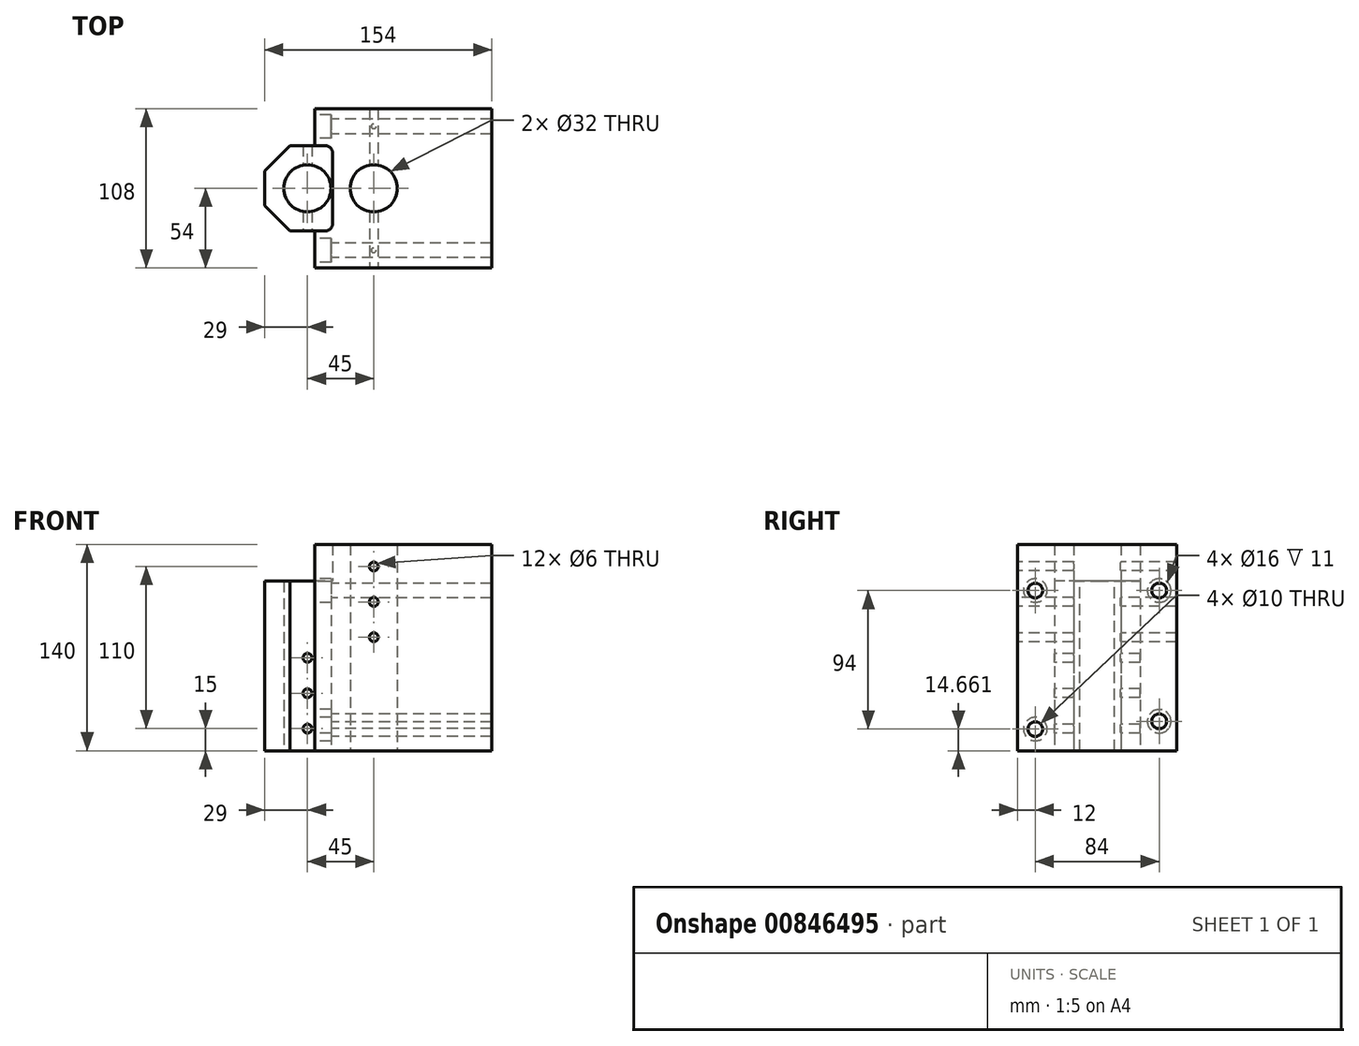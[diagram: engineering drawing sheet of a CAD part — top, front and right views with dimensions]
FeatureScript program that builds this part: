
annotation { "Feature Type Name" : "Feature", "Feature Type Description" : "" }
export const myFeature = defineFeature(function(context is Context, id is Id, definition is map)
    precondition{}
    {
        {
            var Q0;
            Q0=qCreatedBy(makeId("Front.planeOp"),FACE);
            var sketch = newSketch(context, id + "F0", { "sketchPlane" : qUnion([Q0])});
            skLineSegment(sketch, "E0.bottom", {"start": v(0, 77) * mm, "end": v(140, 77) * mm});
            skLineSegment(sketch, "E0.top", {"start": v(0, -77) * mm, "end": v(140, -77) * mm});
            skLineSegment(sketch, "E0.left", {"start": v(0, 77) * mm, "end": v(0, -77) * mm});
            skLineSegment(sketch, "E0.right", {"start": v(140, 77) * mm, "end": v(140, -77) * mm});
            skSolve(sketch);
        }
        {
            var Q0;
            Q0 = qSketchRegion(id + "F0", true);
            extrude(context, id + "F1", {"entities" : qUnion([Q0]), "endBound" : BoundingType.SYMMETRIC, "depth" : 108 * mm, "offsetDistance" : 25 * mm});
        }
        {
            var Q0;
            Q0=makeQuery(id+"F1.opExtrude","SWEPT_FACE",FACE,{"disambiguationData":[OSD([sQuery(id+"F0.wireOp",EDGE,"E0.left")])]});
            var sketch = newSketch(context, id + "F2", { "sketchPlane" : qUnion([Q0])});
            skCircle(sketch, "E1", {"center": v(0, 48) * mm, "radius": 16 * mm});
            skCircle(sketch, "E2", {"center": v(0, 3) * mm, "radius": 16 * mm});
            skLineSegment(sketch, "E3", {"start": v(0, -11.7) * mm, "end": v(0, 60.82) * mm, "construction": true});
            skSolve(sketch);
        }
        {
            var Q0;
            Q0 = qSketchRegion(id + "F2", true);
            extrude(context, id + "F3", {"entities" : qUnion([Q0]), "operationType" : NewBodyOperationType.REMOVE, "endBound" : BoundingType.THROUGH_ALL, "oppositeDirection" : true, "depth" : 25 * mm, "offsetDistance" : 25 * mm});
        }
        {
            var Q0;
            Q0=makeQuery(id+"F1.opExtrude","SWEPT_FACE",FACE,{"disambiguationData":[OSD([sQuery(id+"F0.wireOp",EDGE,"E0.left")])]});
            var sketch = newSketch(context, id + "F4", { "sketchPlane" : qUnion([Q0])});
            skLineSegment(sketch, "E4", {"start": v(-54, 43) * mm, "end": v(-29, 43) * mm});
            skLineSegment(sketch, "E5", {"start": v(-29, 43) * mm, "end": v(-29, 59.73) * mm});
            skLineSegment(sketch, "E6", {"start": v(-29, 59.73) * mm, "end": v(-11.7, 77.04) * mm});
            skLineSegment(sketch, "E7", {"start": v(-11.7, 77.04) * mm, "end": v(0, 77.04) * mm});
            skLineSegment(sketch, "E8", {"start": v(0, 7.7) * mm, "end": v(0, 92.54) * mm, "construction": true});
            skPoint(sketch, "E8.startSnap0", {"position": v(0, 77) * mm});
            skLineSegment(sketch, "E9.MirrorCS", {"start": v(11.7, 77.04) * mm, "end": v(0, 77.04) * mm});
            skLineSegment(sketch, "E10.MirrorCS", {"start": v(29, 59.73) * mm, "end": v(11.7, 77.04) * mm});
            skLineSegment(sketch, "E11.MirrorCS", {"start": v(54, 43) * mm, "end": v(29, 43) * mm});
            skLineSegment(sketch, "E12.MirrorCS", {"start": v(29, 43) * mm, "end": v(29, 59.73) * mm});
            skLineSegment(sketch, "E13", {"start": v(-54, 43) * mm, "end": v(-54, 77) * mm});
            skLineSegment(sketch, "E14", {"start": v(-54, 77) * mm, "end": v(-11.7, 77.04) * mm});
            skLineSegment(sketch, "E15", {"start": v(54, 77) * mm, "end": v(11.7, 77.04) * mm});
            skLineSegment(sketch, "E16", {"start": v(54, 77) * mm, "end": v(54, 43) * mm});
            skSolve(sketch);
        }
        {
            var Q0;
            Q0 = qSketchRegion(id + "F4", true);
            extrude(context, id + "F5", {"entities" : qUnion([Q0]), "operationType" : NewBodyOperationType.REMOVE, "endBound" : BoundingType.THROUGH_ALL, "oppositeDirection" : true, "depth" : 25 * mm, "offsetDistance" : 25 * mm});
        }
        {
            var Q0;
            Q0=makeQuery(id+"F1.opExtrude","SWEPT_FACE",FACE,{"disambiguationData":[OSD([sQuery(id+"F0.wireOp",EDGE,"E0.bottom")])]});
            var sketch = newSketch(context, id + "F6", { "sketchPlane" : qUnion([Q0])});
            skLineSegment(sketch, "E17", {"start": v(140, 29) * mm, "end": v(140, -29) * mm});
            skLineSegment(sketch, "E18", {"start": v(115, 29) * mm, "end": v(115, -29) * mm});
            skPoint(sketch, "E19.orphan", {"position": v(0, 54) * mm});
            skPoint(sketch, "E20.orphan", {"position": v(0, -54) * mm});
            skLineSegment(sketch, "E21.0", {"start": v(140, 29) * mm, "end": v(115, 29) * mm});
            skLineSegment(sketch, "E22.0", {"start": v(140, -29) * mm, "end": v(115, -29) * mm});
            skPoint(sketch, "E23.orphan", {"position": v(0, -29) * mm});
            skPoint(sketch, "E24.orphan", {"position": v(140, -54) * mm});
            skPoint(sketch, "E25.0.start.orphan", {"position": v(140, 54) * mm});
            skPoint(sketch, "E26.orphan", {"position": v(0, 29) * mm});
            skSolve(sketch);
        }
        {
            var Q0;
            Q0 = qSketchRegion(id + "F6", true);
            extrude(context, id + "F7", {"entities" : qUnion([Q0]), "operationType" : NewBodyOperationType.REMOVE, "oppositeDirection" : true, "depth" : 46 * mm, "offsetDistance" : 25 * mm});
        }
        {
            var Q0;
            Q0=makeQuery(id+"F7.boolean.opBoolean","COPY",EDGE,{"derivedFrom":makeQuery(id+"F7.opExtrude","CAP_EDGE",EDGE,{"disambiguationData":[OSD([sQuery(id+"F6.wireOp",EDGE,"E22.0")])],"isStart":false})});
            var Q1;
            Q1=makeQuery(id+"F7.boolean.opBoolean","COPY",EDGE,{"derivedFrom":makeQuery(id+"F7.opExtrude","CAP_EDGE",EDGE,{"disambiguationData":[OSD([sQuery(id+"F6.wireOp",EDGE,"E21.0")])],"isStart":false})});
            fillet(context, id + "F8", {"entities" : qUnion([Q0, Q1]), "radius" : 5 * mm, "tangentPropagation" : true, "allowEdgeOverflow" : false});
        }
        {
            var Q0;
            Q0=makeQuery(id+"F1.opExtrude","SWEPT_BODY",BODY,{"disambiguationData":[OSD([sQuery(id+"F0.wireOp",EDGE,"E0.bottom"),sQuery(id+"F0.wireOp",EDGE,"E0.top"),sQuery(id+"F0.wireOp",EDGE,"E0.left"),sQuery(id+"F0.wireOp",EDGE,"E0.right")])]});
            var Q1;
            Q1=makeQuery(id+"F1.opExtrude","SWEPT_EDGE",EDGE,{"disambiguationData":[OSD([sQuery(id+"F0.wireOp",EDGE,"E0.top"),sQuery(id+"F0.wireOp",EDGE,"E0.left")])]});
            transform(context, id + "F9", {"entities" : qUnion([Q0]), "transformType" : TransformType.ROTATION, "transformAxis" : qUnion([Q1]), "angle" : 270 * degree, "makeCopy" : false});
        }
        {
            var Q0;
            Q0=makeQuery(id+"F1.opExtrude","SWEPT_FACE",FACE,{"disambiguationData":[OSD([sQuery(id+"F0.wireOp",EDGE,"E0.left")])]});
            var sketch = newSketch(context, id + "F10", { "sketchPlane" : qUnion([Q0])});
            skLineSegment(sketch, "E27", {"start": v(0, 0) * mm, "end": v(-154, 0) * mm, "construction": true});
            skSolve(sketch);
        }
        {
            var Q0;
            Q0=makeQuery(id+"F1.opExtrude","SWEPT_BODY",BODY,{"disambiguationData":[OSD([sQuery(id+"F0.wireOp",EDGE,"E0.bottom"),sQuery(id+"F0.wireOp",EDGE,"E0.top"),sQuery(id+"F0.wireOp",EDGE,"E0.left"),sQuery(id+"F0.wireOp",EDGE,"E0.right")])]});
            var Q1;
            Q1=sQuery(id+"F10.wireOp",EDGE,"E27");
            transform(context, id + "F11", {"entities" : qUnion([Q0]), "transformType" : TransformType.TRANSLATION_ENTITY, "oppositeDirectionEntity" : true, "transformLine" : qUnion([Q1]), "makeCopy" : false});
        }
        {
            var Q0;
            Q0=makeQuery(id+"F1.opExtrude","SWEPT_FACE",FACE,{"disambiguationData":[OSD([sQuery(id+"F0.wireOp",EDGE,"E0.top")])]});
            var sketch = newSketch(context, id + "F12", { "sketchPlane" : qUnion([Q0])});
            skLineSegment(sketch, "E28", {"start": v(-54, -77) * mm, "end": v(54, 63) * mm, "construction": true});
            skPoint(sketch, "E29", {"position": v(0, 0) * mm});
            skPoint(sketch, "E30", {"position": v(0, -7) * mm});
            skLineSegment(sketch, "E31", {"start": v(0, -7) * mm, "end": v(0, 0) * mm, "construction": true});
            skSolve(sketch);
        }
        {
            var Q0;
            Q0=makeQuery(id+"F1.opExtrude","SWEPT_BODY",BODY,{"disambiguationData":[OSD([sQuery(id+"F0.wireOp",EDGE,"E0.bottom"),sQuery(id+"F0.wireOp",EDGE,"E0.top"),sQuery(id+"F0.wireOp",EDGE,"E0.left"),sQuery(id+"F0.wireOp",EDGE,"E0.right")])]});
            var Q1;
            Q1=sQuery(id+"F12.wireOp",EDGE,"E31");
            transform(context, id + "F13", {"entities" : qUnion([Q0]), "transformType" : TransformType.TRANSLATION_ENTITY, "oppositeDirectionEntity" : false, "transformLine" : qUnion([Q1]), "makeCopy" : false});
        }
        {
            var Q0;
            Q0=makeQuery(id+"F1.opExtrude","SWEPT_FACE",FACE,{"disambiguationData":[OSD([sQuery(id+"F0.wireOp",EDGE,"E0.bottom")])]});
            var sketch = newSketch(context, id + "F14", { "sketchPlane" : qUnion([Q0])});
            skCircle(sketch, "E32", {"center": v(42, 38.66) * mm, "radius": 8 * mm});
            skCircle(sketch, "E33", {"center": v(-42, 38.66) * mm, "radius": 8 * mm});
            skCircle(sketch, "E34", {"center": v(42, -55.34) * mm, "radius": 8 * mm});
            skCircle(sketch, "E35", {"center": v(-42, -50) * mm, "radius": 8 * mm});
            skLineSegment(sketch, "E36", {"start": v(42, 38.66) * mm, "end": v(42, -55.34) * mm, "construction": true});
            skLineSegment(sketch, "E37", {"start": v(42, 38.66) * mm, "end": v(-42, 38.66) * mm, "construction": true});
            skLineSegment(sketch, "E38", {"start": v(-42, 38.66) * mm, "end": v(-42, -50) * mm, "construction": true});
            skSolve(sketch);
        }
        {
            var Q0;
            Q0 = qSketchRegion(id + "F14", true);
            extrude(context, id + "F15", {"entities" : qUnion([Q0]), "operationType" : NewBodyOperationType.REMOVE, "oppositeDirection" : true, "depth" : 45 * mm, "offsetDistance" : 25 * mm});
        }
        {
            var Q0;
            Q0=makeQuery(id+"F5.boolean.opBoolean","COPY",FACE,{"derivedFrom":makeQuery(id+"F5.opExtrude","SWEPT_FACE",FACE,{"disambiguationData":[OSD([sQuery(id+"F4.wireOp",EDGE,"E4")])]})});
            var sketch = newSketch(context, id + "F16", { "sketchPlane" : qUnion([Q0])});
            skCircle(sketch, "E39", {"center": v(-42, -50) * mm, "radius": 5 * mm});
            skCircle(sketch, "E40", {"center": v(-42, 38.66) * mm, "radius": 5 * mm});
            skCircle(sketch, "E41", {"center": v(42, 38.66) * mm, "radius": 5 * mm});
            skCircle(sketch, "E42", {"center": v(42, -55.34) * mm, "radius": 5 * mm});
            skSolve(sketch);
        }
        {
            var Q0;
            Q0 = qSketchRegion(id + "F16", true);
            extrude(context, id + "F17", {"entities" : qUnion([Q0]), "operationType" : NewBodyOperationType.REMOVE, "endBound" : BoundingType.THROUGH_ALL, "oppositeDirection" : true, "depth" : 25 * mm, "offsetDistance" : 25 * mm});
        }
        {
            var Q0;
            Q0=makeQuery(id+"F1.opExtrude","CAP_FACE",FACE,{"disambiguationData":[OSD([sQuery(id+"F0.wireOp",EDGE,"E0.bottom"),sQuery(id+"F0.wireOp",EDGE,"E0.top"),sQuery(id+"F0.wireOp",EDGE,"E0.left"),sQuery(id+"F0.wireOp",EDGE,"E0.right")])],"isStart":false});
            var sketch = newSketch(context, id + "F18", { "sketchPlane" : qUnion([Q0])});
            skLineSegment(sketch, "E43", {"start": v(74, 76.38) * mm, "end": v(74, -76.2) * mm, "construction": true});
            skLineSegment(sketch, "E44", {"start": v(29, 59.3) * mm, "end": v(29, -85.08) * mm, "construction": true});
            skCircle(sketch, "E45", {"center": v(29, -55) * mm, "radius": 3 * mm});
            skCircle(sketch, "E46", {"center": v(29, -31) * mm, "radius": 3 * mm});
            skCircle(sketch, "E47", {"center": v(29, -7) * mm, "radius": 3 * mm});
            skCircle(sketch, "E48", {"center": v(74, 55) * mm, "radius": 3 * mm});
            skCircle(sketch, "E49", {"center": v(74, 31) * mm, "radius": 3 * mm});
            skCircle(sketch, "E50", {"center": v(74, 7) * mm, "radius": 3 * mm});
            skSolve(sketch);
        }
        {
            var Q0;
            Q0 = qSketchRegion(id + "F18", true);
            extrude(context, id + "F19", {"entities" : qUnion([Q0]), "operationType" : NewBodyOperationType.REMOVE, "endBound" : BoundingType.THROUGH_ALL, "oppositeDirection" : true, "depth" : 25 * mm, "offsetDistance" : 25 * mm});
        }
    });
